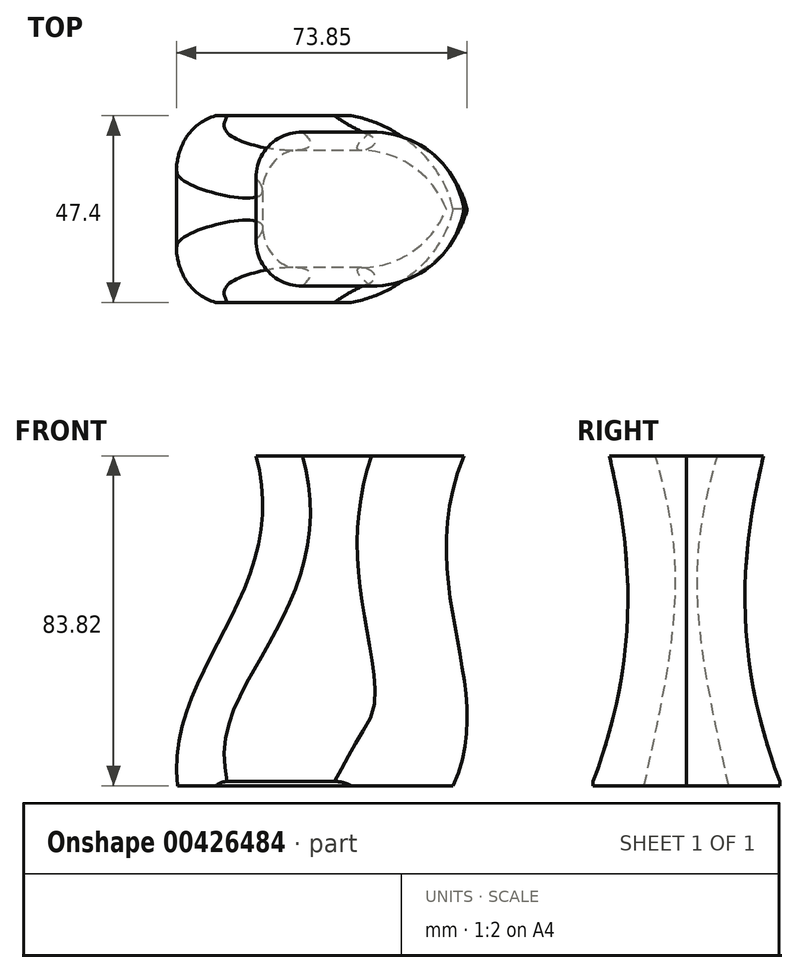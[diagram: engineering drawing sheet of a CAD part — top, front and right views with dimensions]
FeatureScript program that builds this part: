
annotation { "Feature Type Name" : "Feature", "Feature Type Description" : "" }
export const myFeature = defineFeature(function(context is Context, id is Id, definition is map)
    precondition{}
    {
        {
            var Q0;
            Q0=qCreatedBy(makeId("Top.planeOp"),FACE);
            var sketch = newSketch(context, id + "F0", { "sketchPlane" : qUnion([Q0])});
            skLineSegment(sketch, "E0.bottom", {"start": v(49.82, -11.85) * mm, "end": v(-49.82, -11.85) * mm});
            skLineSegment(sketch, "E0.top", {"start": v(49.82, 11.85) * mm, "end": v(-49.82, 11.85) * mm});
            skLineSegment(sketch, "E0.left", {"start": v(49.82, -11.85) * mm, "end": v(49.82, 11.85) * mm});
            skLineSegment(sketch, "E0.right", {"start": v(-49.82, -11.85) * mm, "end": v(-49.82, 11.85) * mm});
            skPoint(sketch, "E0.middle", {"position": v(0, 0) * mm});
            skSolve(sketch);
        }
        {
            var Q0;
            Q0=makeQuery(id+"F0.imprint","IMPRINT",FACE,{"disambiguationData":[TD([[makeQuery(id+"F0.imprint","IMPRINT",EDGE,{"derivedFrom":sQuery(id+"F0.wireOp",EDGE,"E0.bottom")}),-1.0]])]});
            extrude(context, id + "F1", {"entities" : qUnion([Q0]), "depth" : 83.82 * mm, "offsetDistance" : 25.4 * mm});
        }
        {
            var Q0;
            Q0=makeQuery(id+"F1.opExtrude","SWEPT_FACE",FACE,{"disambiguationData":[OSD([sQuery(id+"F0.wireOp",EDGE,"E0.top")])]});
            var sketch = newSketch(context, id + "F2", { "sketchPlane" : qUnion([Q0])});
            skLineSegment(sketch, "E1.bottom", {"start": v(-49.82, 83.82) * mm, "end": v(49.82, 83.82) * mm});
            skLineSegment(sketch, "E1.top", {"start": v(-49.82, 0) * mm, "end": v(49.82, 0) * mm});
            skLineSegment(sketch, "E1.left", {"start": v(-49.82, 83.82) * mm, "end": v(-49.82, 0) * mm});
            skLineSegment(sketch, "E1.right", {"start": v(49.82, 83.82) * mm, "end": v(49.82, 0) * mm});
            skFitSpline(sketch, "E2", {"points": [v(19.66, 83.82) * mm, v(39.59, 0) * mm], "startDerivative": vector(-28.28, -104.72) * mm, "endDerivative": vector(-10.5, -89.37) * mm});
            skFitSpline(sketch, "E3", {"points": [v(-33.12, 83.82) * mm, v(-30.43, 0) * mm], "startDerivative": vector(40.4, -101.5) * mm, "endDerivative": vector(35.55, -76.45) * mm});
            skSolve(sketch);
        }
        {
            var Q0;
            {var subQ0=sQuery(id+"F2.wireOp",EDGE,"E1.right");Q0=makeQuery(id+"F2.imprint","IMPRINT",FACE,{"disambiguationData":[TD([[makeQuery(id+"F2.imprint","IMPRINT",EDGE,{"derivedFrom":subQ0}),-1.0]])]});}
            var Q1;
            {var subQ0=sQuery(id+"F2.wireOp",EDGE,"E1.left");Q1=makeQuery(id+"F2.imprint","IMPRINT",FACE,{"disambiguationData":[TD([[makeQuery(id+"F2.imprint","IMPRINT",EDGE,{"derivedFrom":subQ0}),1.0]])]});}
            extrude(context, id + "F3", {"entities" : qUnion([Q0, Q1]), "operationType" : NewBodyOperationType.REMOVE, "oppositeDirection" : true, "depth" : 40.9 * mm, "offsetDistance" : 25.4 * mm});
        }
        {
            var Q0;
            Q0=qCreatedBy(makeId("Right.planeOp"),FACE);
            cPlane(context, id + "F4", {"entities" : qUnion([Q0]), "cplaneType" : CPlaneType.OFFSET, "offset" : 35.56 * mm, "width" : 152.4 * mm, "height" : 152.4 * mm});
        }
        {
            var Q0;
            Q0=qCreatedBy(id+"F4.planeOp",FACE);
            var sketch = newSketch(context, id + "F5", { "sketchPlane" : qUnion([Q0])});
            skLineSegment(sketch, "E4.bottom", {"start": v(-12.25, 83.84) * mm, "end": v(12.39, 83.84) * mm});
            skLineSegment(sketch, "E4.top", {"start": v(-12.25, 0) * mm, "end": v(12.39, 0) * mm});
            skLineSegment(sketch, "E4.left", {"start": v(-12.25, 83.84) * mm, "end": v(-12.25, 0) * mm});
            skLineSegment(sketch, "E4.right", {"start": v(12.39, 83.84) * mm, "end": v(12.39, 0) * mm});
            skFitSpline(sketch, "E5", {"points": [v(-7.72, 83.84) * mm, v(-12.25, 0) * mm], "startDerivative": vector(18.62, -79.43) * mm, "endDerivative": vector(-36.76, -96.89) * mm});
            skSolve(sketch);
        }
        {
            var Q0;
            {var subQ0=sQuery(id+"F5.wireOp",EDGE,"E4.left");Q0=makeQuery(id+"F5.imprint","IMPRINT",FACE,{"disambiguationData":[TD([[makeQuery(id+"F5.imprint","IMPRINT",EDGE,{"derivedFrom":subQ0}),1.0]])]});}
            extrude(context, id + "F6", {"entities" : qUnion([Q0]), "operationType" : NewBodyOperationType.REMOVE, "oppositeDirection" : true, "depth" : 103.12 * mm, "offsetDistance" : 25.4 * mm});
        }
        {
            var Q0;
            Q0=makeQuery(id+"F6.boolean.opBoolean","INTERSECT",EDGE,{"derivedFrom":[makeQuery(id+"F3.boolean.opBoolean","COPY",FACE,{"derivedFrom":makeQuery(id+"F3.opExtrude","SWEPT_FACE",FACE,{"disambiguationData":[OSD([sQuery(id+"F2.wireOp",EDGE,"E2")])]})}),makeQuery(id+"F6.opExtrude","SWEPT_FACE",FACE,{"disambiguationData":[OSD([sQuery(id+"F5.wireOp",EDGE,"E5")])]})]});
            fillet(context, id + "F7", {"entities" : qUnion([Q0]), "radius" : 12.1 * mm, "tangentPropagation" : true, "allowEdgeOverflow" : false});
        }
        {
            var Q0;
            Q0=makeQuery(id+"F6.boolean.opBoolean","INTERSECT",EDGE,{"derivedFrom":[makeQuery(id+"F3.boolean.opBoolean","COPY",FACE,{"derivedFrom":makeQuery(id+"F3.opExtrude","SWEPT_FACE",FACE,{"disambiguationData":[OSD([sQuery(id+"F2.wireOp",EDGE,"E3")])]})}),makeQuery(id+"F6.opExtrude","SWEPT_FACE",FACE,{"disambiguationData":[OSD([sQuery(id+"F5.wireOp",EDGE,"E5")])]})]});
            fillet(context, id + "F8", {"entities" : qUnion([Q0]), "radius" : 24.23 * mm, "tangentPropagation" : true, "allowEdgeOverflow" : false});
        }
        {
            var Q0;
            Q0=makeQuery(id+"F1.opExtrude","SWEPT_BODY",BODY,{"disambiguationData":[OSD([sQuery(id+"F0.wireOp",EDGE,"E0.bottom"),sQuery(id+"F0.wireOp",EDGE,"E0.top"),sQuery(id+"F0.wireOp",EDGE,"E0.left"),sQuery(id+"F0.wireOp",EDGE,"E0.right")])]});
            var Q1;
            Q1=makeQuery(id+"F1.opExtrude","SWEPT_FACE",FACE,{"disambiguationData":[OSD([sQuery(id+"F0.wireOp",EDGE,"E0.top")])]});
            mirror(context, id + "F9", {"operationType" : NewBodyOperationType.ADD, "entities" : qUnion([Q0]), "mirrorPlane" : qUnion([Q1])});
        }
    });
